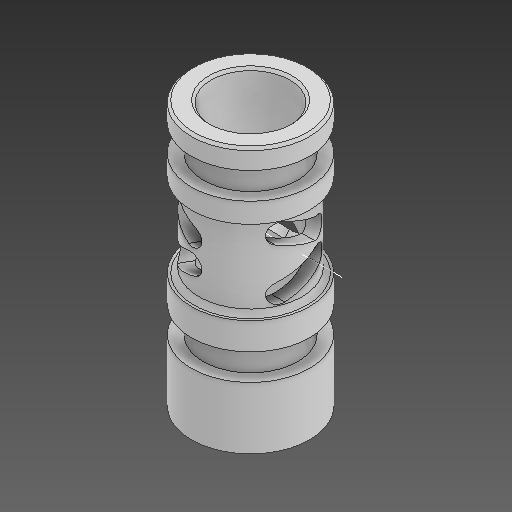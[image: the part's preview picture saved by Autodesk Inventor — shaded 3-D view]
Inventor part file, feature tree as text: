
AUTODESK INVENTOR PART (.ipt)
format: ipt  version: 2021 (Build 250183000, 183)  size: 310,784 bytes
history: native  units: in
note: dims shown in document units (in); Inventor stores cm internally (conversion verified against a paired STEP export)
features: other x7, sketch x5, plane x1
ambient origin geometry x8: Origin, YZ Plane, XZ Plane, XY Plane, X Axis, Y Axis, Z Axis, Center Point
bodies: Solid1 (feature_tree)
feature tree (13):
  other  "outer_sleeve.ipt"
  other  "Solid1::outer_sleeve.ipt"
  other  "TaggingFeature1"
  sketch  "Sketch2"  dims[d0=0.3937in]
  sketch  "Sketch3"
  sketch  "Sketch4"
  sketch  "Sketch5"
  sketch  "Sketch10"
  plane  "Work Plane1"
  other  "Work Axis1"
  other  "Work Axis2"
  other  "Srf1"
  other  "Srf1::Derived"
